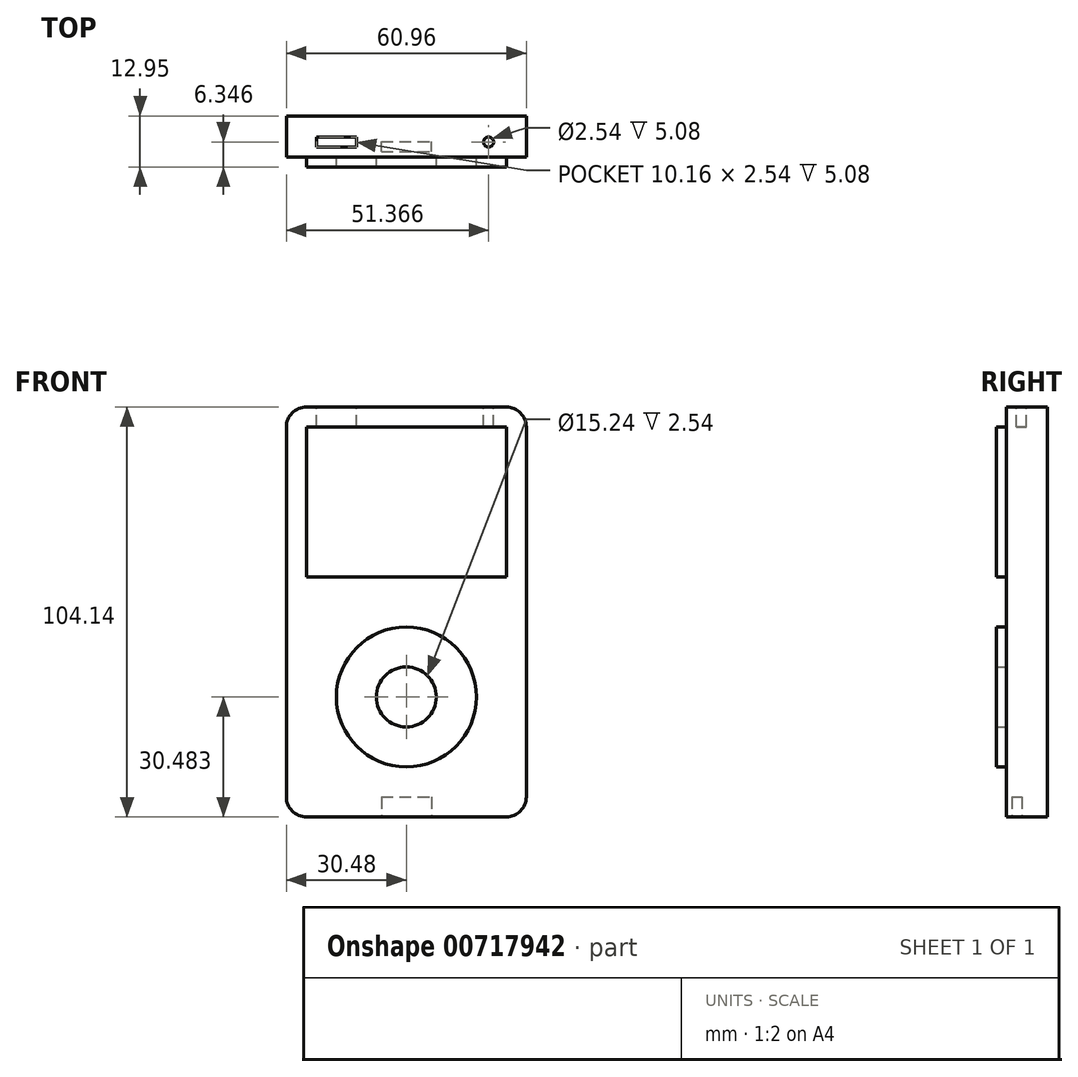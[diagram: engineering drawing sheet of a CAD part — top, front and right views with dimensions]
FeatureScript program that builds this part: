
annotation { "Feature Type Name" : "Feature", "Feature Type Description" : "" }
export const myFeature = defineFeature(function(context is Context, id is Id, definition is map)
    precondition{}
    {
        {
            var Q0;
            Q0=qCreatedBy(makeId("Front.planeOp"),FACE);
            var sketch = newSketch(context, id + "F0", { "sketchPlane" : qUnion([Q0])});
            skLineSegment(sketch, "E0.bottom", {"start": v(-55.88, 57.66) * mm, "end": v(-5.08, 57.66) * mm});
            skLineSegment(sketch, "E0.top", {"start": v(-55.88, -46.48) * mm, "end": v(-5.08, -46.48) * mm});
            skLineSegment(sketch, "E0.left", {"start": v(-60.96, 52.58) * mm, "end": v(-60.96, -41.4) * mm});
            skLineSegment(sketch, "E0.right", {"start": v(0, 52.58) * mm, "end": v(0, -41.4) * mm});
            skPoint(sketch, "E1.visualSharp", {"position": v(-60.96, 57.66) * mm});
            skArc(sketch, "E1.filletArc", {"start": v(-55.88, 57.66) * mm, "mid": v(-59.47, 56.17) * mm, "end": v(-60.96, 52.58) * mm});
            skPoint(sketch, "E2.visualSharp", {"position": v(-60.96, -46.48) * mm});
            skArc(sketch, "E2.filletArc", {"start": v(-60.96, -41.4) * mm, "mid": v(-59.47, -44.99) * mm, "end": v(-55.88, -46.48) * mm});
            skPoint(sketch, "E3.visualSharp", {"position": v(0, -46.48) * mm});
            skArc(sketch, "E3.filletArc", {"start": v(-5.08, -46.48) * mm, "mid": v(-1.49, -44.99) * mm, "end": v(0, -41.4) * mm});
            skPoint(sketch, "E4.visualSharp", {"position": v(0, 57.66) * mm});
            skArc(sketch, "E4.filletArc", {"start": v(0, 52.58) * mm, "mid": v(-1.49, 56.17) * mm, "end": v(-5.08, 57.66) * mm});
            skPoint(sketch, "E5.middle", {"position": v(-30.48, 32.26) * mm});
            skPoint(sketch, "E6.oppositeSnap0", {"position": v(0, 65.28) * mm});
            skPoint(sketch, "E7.visualSharp", {"position": v(-60.96, 70.36) * mm});
            skPoint(sketch, "E8.visualSharp", {"position": v(0, 70.36) * mm});
            skPoint(sketch, "E9.visualSharp", {"position": v(0, -59.18) * mm});
            skPoint(sketch, "E10.visualSharp", {"position": v(-60.96, -59.18) * mm});
            skPoint(sketch, "E11.middle", {"position": v(-30.48, -51.65) * mm});
            skPoint(sketch, "E12.middle", {"position": v(-54.77, 62.21) * mm});
            skPoint(sketch, "E12.right.start.orphan", {"position": v(-51.44, 61.54) * mm});
            skPoint(sketch, "E12.top.end.orphan", {"position": v(-51.44, 62.9) * mm});
            skPoint(sketch, "E12.left.end.orphan", {"position": v(-58.1, 62.9) * mm});
            skPoint(sketch, "E12.left.start.orphan", {"position": v(-58.1, 61.54) * mm});
            skPoint(sketch, "E13.left.start.orphan", {"position": v(-60.96, 60.2) * mm});
            skPoint(sketch, "E14.orphan", {"position": v(0, 60.2) * mm});
            skPoint(sketch, "E11.left.end.orphan", {"position": v(-37.73, -50.35) * mm});
            skPoint(sketch, "E11.bottom.start.orphan", {"position": v(-37.73, -52.96) * mm});
            skPoint(sketch, "E11.right.end.orphan", {"position": v(-23.23, -50.35) * mm});
            skPoint(sketch, "E11.right.start.orphan", {"position": v(-23.23, -52.96) * mm});
            skPoint(sketch, "E6.right.start.orphan", {"position": v(0, -49.02) * mm});
            skPoint(sketch, "E6.left.start.orphan", {"position": v(-60.96, -49.02) * mm});
            skPoint(sketch, "E15.center.orphan", {"position": v(-30.48, -16) * mm});
            skPoint(sketch, "E5.right.end.orphan", {"position": v(-5.08, 13.21) * mm});
            skPoint(sketch, "E5.left.end.orphan", {"position": v(-55.88, 13.21) * mm});
            skPoint(sketch, "E5.bottom.end.orphan", {"position": v(-5.08, 51.31) * mm});
            skPoint(sketch, "E5.bottom.start.orphan", {"position": v(-55.88, 51.31) * mm});
            skSolve(sketch);
        }
        {
            var Q0;
            Q0=makeQuery(id+"F0.imprint","IMPRINT",FACE,{"disambiguationData":[TD([[makeQuery(id+"F0.imprint","IMPRINT",EDGE,{"derivedFrom":sQuery(id+"F0.wireOp",EDGE,"E0.bottom")}),-1.0]])]});
            extrude(context, id + "F1", {"entities" : qUnion([Q0]), "depth" : 10.4 * mm, "offsetDistance" : 25.4 * mm});
        }
        {
            var Q0;
            Q0=makeQuery(id+"F1.opExtrude","CAP_FACE",FACE,{"disambiguationData":[OSD([sQuery(id+"F0.wireOp",EDGE,"E0.bottom"),sQuery(id+"F0.wireOp",EDGE,"E0.top"),sQuery(id+"F0.wireOp",EDGE,"E0.left"),sQuery(id+"F0.wireOp",EDGE,"E0.right"),sQuery(id+"F0.wireOp",EDGE,"E1.filletArc"),sQuery(id+"F0.wireOp",EDGE,"E2.filletArc"),sQuery(id+"F0.wireOp",EDGE,"E3.filletArc"),sQuery(id+"F0.wireOp",EDGE,"E4.filletArc")])],"isStart":false});
            var sketch = newSketch(context, id + "F2", { "sketchPlane" : qUnion([Q0])});
            skLineSegment(sketch, "E16.bottom", {"start": v(-55.88, 52.58) * mm, "end": v(-5.08, 52.58) * mm});
            skLineSegment(sketch, "E16.top", {"start": v(-55.88, 14.48) * mm, "end": v(-5.08, 14.48) * mm});
            skLineSegment(sketch, "E16.left", {"start": v(-55.88, 52.58) * mm, "end": v(-55.88, 14.48) * mm});
            skLineSegment(sketch, "E16.right", {"start": v(-5.08, 52.58) * mm, "end": v(-5.08, 14.48) * mm});
            skCircle(sketch, "E17", {"center": v(-30.48, -16) * mm, "radius": 17.78 * mm});
            skCircle(sketch, "E18", {"center": v(-30.48, -16) * mm, "radius": 7.62 * mm});
            skSolve(sketch);
        }
        {
            var Q0;
            Q0 = qSketchRegion(id + "F2", true);
            extrude(context, id + "F3", {"entities" : qUnion([Q0]), "operationType" : NewBodyOperationType.ADD, "depth" : 2.54 * mm, "offsetDistance" : 25.4 * mm});
        }
        {
            var Q0;
            Q0=makeQuery(id+"F1.opExtrude","SWEPT_FACE",FACE,{"disambiguationData":[OSD([sQuery(id+"F0.wireOp",EDGE,"E0.bottom")])]});
            var sketch = newSketch(context, id + "F4", { "sketchPlane" : qUnion([Q0])});
            skPoint(sketch, "E19.firstSnap0", {"position": v(-55.88, -5.33) * mm});
            skLineSegment(sketch, "E19.bottom", {"start": v(-53.34, -5.33) * mm, "end": v(-43.18, -5.33) * mm});
            skLineSegment(sketch, "E19.top", {"start": v(-53.34, -7.87) * mm, "end": v(-43.18, -7.87) * mm});
            skLineSegment(sketch, "E19.left", {"start": v(-53.34, -5.33) * mm, "end": v(-53.34, -7.87) * mm});
            skLineSegment(sketch, "E19.right", {"start": v(-43.18, -5.33) * mm, "end": v(-43.18, -7.87) * mm});
            skCircle(sketch, "E20", {"center": v(-9.6, -6.6) * mm, "radius": 1.27 * mm});
            skSolve(sketch);
        }
        {
            var Q0;
            Q0 = qSketchRegion(id + "F4", true);
            extrude(context, id + "F5", {"entities" : qUnion([Q0]), "operationType" : NewBodyOperationType.REMOVE, "oppositeDirection" : true, "depth" : 5.08 * mm, "offsetDistance" : 25.4 * mm});
        }
        {
            var Q0;
            Q0=makeQuery(id+"F1.opExtrude","SWEPT_FACE",FACE,{"disambiguationData":[OSD([sQuery(id+"F0.wireOp",EDGE,"E0.top")])]});
            var sketch = newSketch(context, id + "F6", { "sketchPlane" : qUnion([Q0])});
            skLineSegment(sketch, "E21.bottom", {"start": v(-36.83, 9.07) * mm, "end": v(-24.13, 9.07) * mm});
            skLineSegment(sketch, "E21.top", {"start": v(-36.83, 6.53) * mm, "end": v(-24.13, 6.53) * mm});
            skLineSegment(sketch, "E21.left", {"start": v(-36.83, 9.07) * mm, "end": v(-36.83, 6.53) * mm});
            skLineSegment(sketch, "E21.right", {"start": v(-24.13, 9.07) * mm, "end": v(-24.13, 6.53) * mm});
            skSolve(sketch);
        }
        {
            var Q0;
            Q0=makeQuery(id+"F6.imprint","IMPRINT",FACE,{"disambiguationData":[TD([[makeQuery(id+"F6.imprint","IMPRINT",EDGE,{"derivedFrom":sQuery(id+"F6.wireOp",EDGE,"E21.bottom")}),-1.0]])]});
            extrude(context, id + "F7", {"entities" : qUnion([Q0]), "operationType" : NewBodyOperationType.REMOVE, "oppositeDirection" : true, "depth" : 5.08 * mm, "offsetDistance" : 25.4 * mm});
        }
    });
